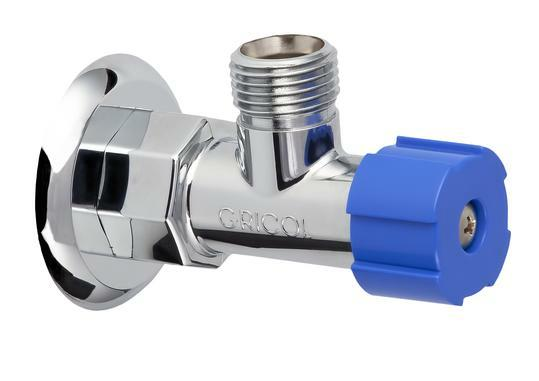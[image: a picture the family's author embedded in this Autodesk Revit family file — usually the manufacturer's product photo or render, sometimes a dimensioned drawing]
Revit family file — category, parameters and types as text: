
# Revit family: BIM_01-3201-09
name_source: partatom
category: Plumbing Fixtures
units: mm (PartAtom-declared; Revit-internal decimal feet)

## family parameters
Classification Number = 23.31.11.00
Cut with Voids When Loaded = No
Enable Cutting in Views = No
Host = Face
Maintain Annotation Orientation = No
Part Type = Normal
Room Calculation Point = No
Round Connector Dimension = Use Diameter
Shared = No

## types (1)
- 01-3201-09
    Ancho = 83.5 mm  [stored 0.27395 ft]
    CW Connection = Yes
    Conexiones = Acometida: Rosca Hembra 1/2” NPT. Salida:
Rosca Macho 1/2” NPSM.
    Date Modified = 22/08/2025
    Default Elevation = 0 mm  [stored 0 ft]
    Description = Llave
    Diametro escudo = 50.6 mm  [stored 0.16601 ft]
    Diametro nominal = 15.9 mm
    Garantia Especifica = 20 AÑOS
    HW Connection = Yes
    Link Ficha Tecnica = https://infotecnica.gricol.com
    Manufacturer = Gricol
    Materiales del producto = ABS, Latón, Caucho
    Model = 01-3201-09
    Plastico - ABS + Colorante azul = Plastico - ABS + Colorante azul
    Plastico - ABS Cromado = Plastico ABS Cromado
    Presión Maxima = 125.00 psi
    Presión Mínima = 20.00 psi
    Presión de Estallído = 500.00 psi
    Product Name = Llave De Regulación Cromada Manija Azul
    Referente Normativo = NTC 1644, ASME A112.18.1 / CSA B125.1
    Rosca NPSM 1/2" = 1/2"
    Rosca NPT 1/2" = 1/2"
    Sitio web = https://www.gricol.com
    Temperaturas de trabajo = DE 5° A 71°
    Tipo de Uso = Domestico
    Torque de Conexión = 61 Nm
    Torque de operación = 1.7 Nm
    Type Image = LLAVE DE REGULACION CRAMADA AZUL.jpg
    URL = https://www.gricol.com
    Vent Connection = No
    Vida Util = 2000 CICLOS
    Waste Connection = No

note: [stored X ft] marks values corroborated as IEEE doubles in the binary element streams (Revit-internal decimal feet)

## geometry (parser evidence)
native form markers: Blend x4, Sweep x5
no freeform markers — native parametric forms only
